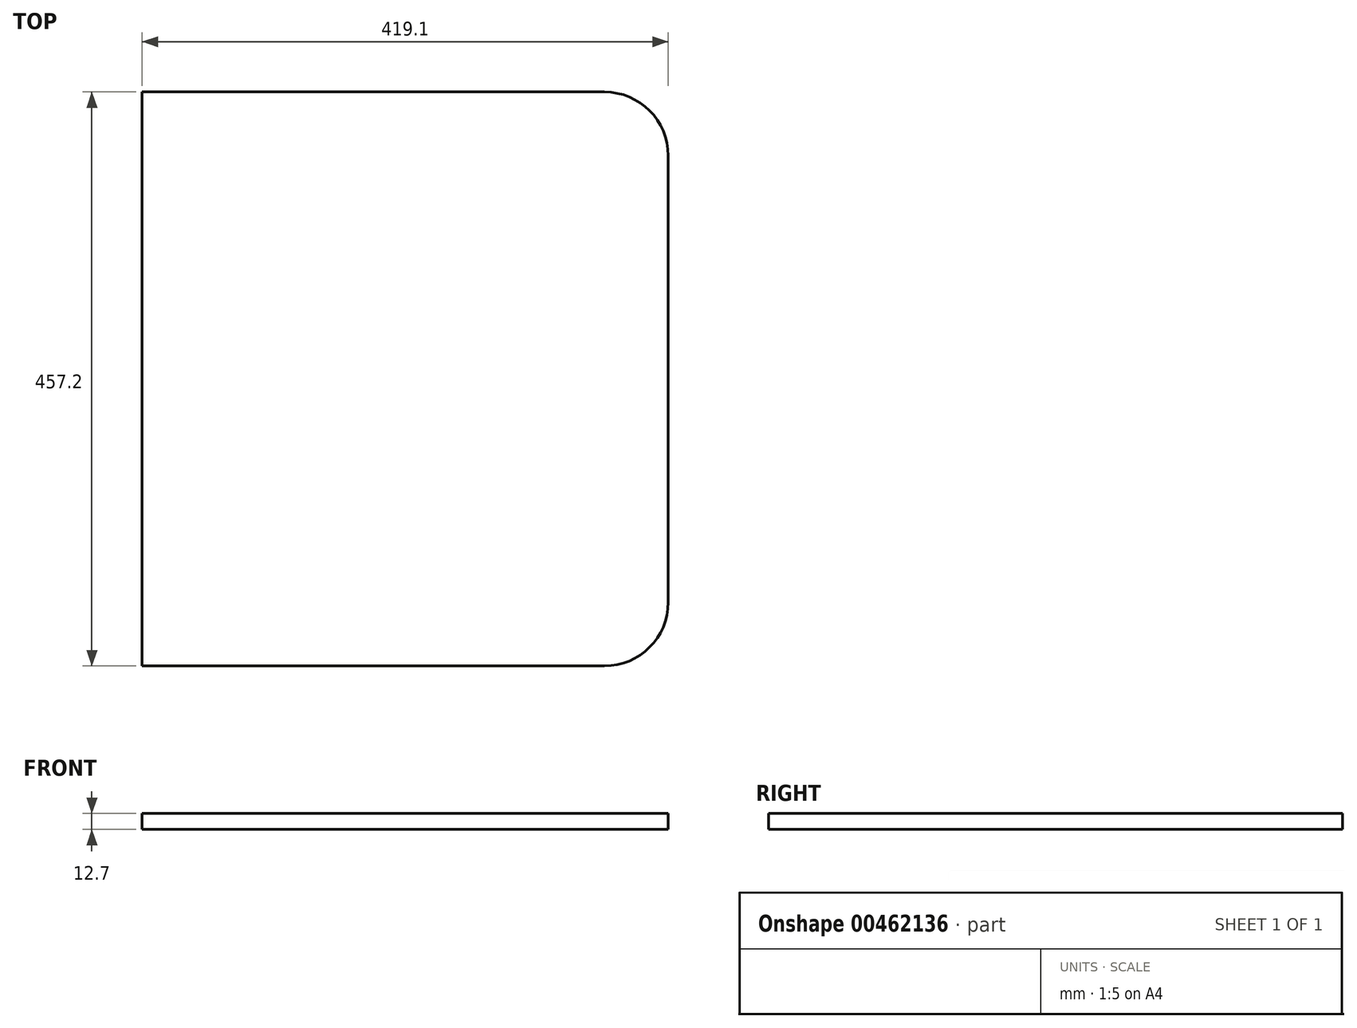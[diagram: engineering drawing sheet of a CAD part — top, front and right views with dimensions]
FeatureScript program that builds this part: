
annotation { "Feature Type Name" : "Feature", "Feature Type Description" : "" }
export const myFeature = defineFeature(function(context is Context, id is Id, definition is map)
    precondition{}
    {
        {
            var Q0;
            Q0=qCreatedBy(makeId("Top.planeOp"),FACE);
            var sketch = newSketch(context, id + "F0", { "sketchPlane" : qUnion([Q0])});
            skLineSegment(sketch, "E0.bottom", {"start": v(0, 0) * mm, "end": v(419.1, 0) * mm});
            skLineSegment(sketch, "E0.top", {"start": v(0, 457.2) * mm, "end": v(419.1, 457.2) * mm});
            skLineSegment(sketch, "E0.left", {"start": v(0, 0) * mm, "end": v(0, 457.2) * mm});
            skLineSegment(sketch, "E0.right", {"start": v(419.1, 0) * mm, "end": v(419.1, 457.2) * mm});
            skSolve(sketch);
        }
        {
            var Q0;
            Q0 = qSketchRegion(id + "F0", true);
            extrude(context, id + "F1", {"entities" : qUnion([Q0]), "depth" : 12.7 * mm});
        }
        {
            var Q0;
            Q0=makeQuery(id+"F1.opExtrude","SWEPT_EDGE",EDGE,{"disambiguationData":[OSD([sQuery(id+"F0.wireOp",EDGE,"E0.top"),sQuery(id+"F0.wireOp",EDGE,"E0.right")])]});
            var Q1;
            Q1=makeQuery(id+"F1.opExtrude","SWEPT_EDGE",EDGE,{"disambiguationData":[OSD([sQuery(id+"F0.wireOp",EDGE,"E0.bottom"),sQuery(id+"F0.wireOp",EDGE,"E0.right")])]});
            fillet(context, id + "F2", {"entities" : qUnion([Q0, Q1]), "radius" : 50.8 * mm, "tangentPropagation" : true, "allowEdgeOverflow" : false});
        }
    });
